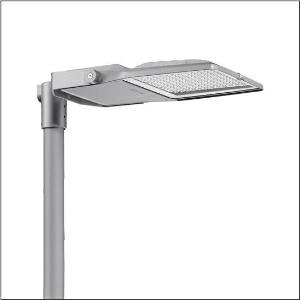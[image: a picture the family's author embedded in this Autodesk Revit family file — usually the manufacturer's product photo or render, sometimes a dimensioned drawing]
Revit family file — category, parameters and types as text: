
# Revit family: floodlight_fl_21_midi___pl43_5xa7786f2a3a_0f3f
name_source: partatom
category: Lighting Fixtures
units: mm (PartAtom-declared; Revit-internal decimal feet)

## family parameters
Cut with Voids When Loaded = No
Host = Face
Light Source = No
Part Type = Normal
Room Calculation Point = No
Round Connector Dimension = Use Diameter
Shared = No

## types (1)
- --- (1 x LED, 36680 lm, 271.6 W, 3000K)
    Apparent Load = 272 VA
    CIE Flux Codes = 27 78 99 100 100
    Color Rendering = 70
    Color Temperature = 3000K
    Default Elevation = 1800 mm
    Description = Floodlight FL 21 midi, floodlight, primary light control with lens, of PMMA, primary optical cover: protective disc, of toughened safety glass, transparent, light distribution: PL43, light emission: direct distribution, installation type: surface-mounted, LED, High Power LED, rated luminous flux: 36.680lm, luminous efficacy: 135lm/W, light colour: 730, colour temperature: 3000K, control gear: ECG Smart Interface, control: flexible luminous flux parameterisation, time-dependent luminous flux control, constant luminous flux control, overheat protection, pre-setting: logarithmic dimming characteristic, with terminal, 6-pole, mains connection: 220..240V, AC, 50/60Hz, start of lifetime: 272W, end of service life: 287W, reduction: 123W, luminaire housing, of diecast aluminium, powder-coated, Siteco® metallic grey (DB 702S), corrosivity category C5 mid according to DIN EN ISO 12944, sealing non-destructively replaceable, please order mast flange separately, mast bracket, of steel, galvanised, powder-coated, Siteco® metallic grey (DB 702S), Smart Interface below and above, protection rating (complete): IP66, insulation class (complete): insulation class II (safety insulation), certification: CE, ENEC, VDE, protection symbol: D, impact resistance: IK08, permissible operating ambient temperature: -40..+40°C, permissible operating ambient temperature for outdoor applications: -40..+50°C, standard: DIN EN 12944, LABS conformity tested according to VDMA 24364:2018-05, packaging unit: 1 piece

Light Distribution: PL43
    Height = 76 mm
    Lamp = 1 x LED
    Lamp Light Flux = 36680 lm
    Lamp Power = 271.6 W
    Lamp count = 1
    Length = 657 mm
    Luminous efficacy = 135 lm/W
    Manufacturer = Siteco
    ModVariant = No
    Model = 5XA7786F2A3A
    Number of Poles = 1
    OnlyDefault = Yes
    Power Factor = 1
    Product Name = Floodlight FL 21 midi | PL43
    Product group = floodlight | pylon annexe
    ProductGroupID = 6200
    Protection Class = Protection class II
    Protection Degree = IP 66
    RLX_Detail_Level = 1
    RLX_Emergency_Light_Flux = 0 lm
    RLX_Emergency_Type = 0
    RLX_Emergency_Type_DB = No
    RlxData = <blob elided: 153677 chars, md5=3d5c467e>
    Socket = socket
    Standby Power = 0 W
    System Light Flux = 36680 lm
    System Power = 272 W
    Type Comments = factory setting: luminous flux: 100 % | dim-lin: 254 | 620 mA
    Type Image = l_1007123.jpg
    URL = http://relux.com
    VarID = @adj_148383
    Voltage = 0 V
    Weight = 0.00 kg
    Width = 442 mm

## geometry (parser evidence)
native form markers: Blend x4, Sweep x14
no freeform markers — native parametric forms only
